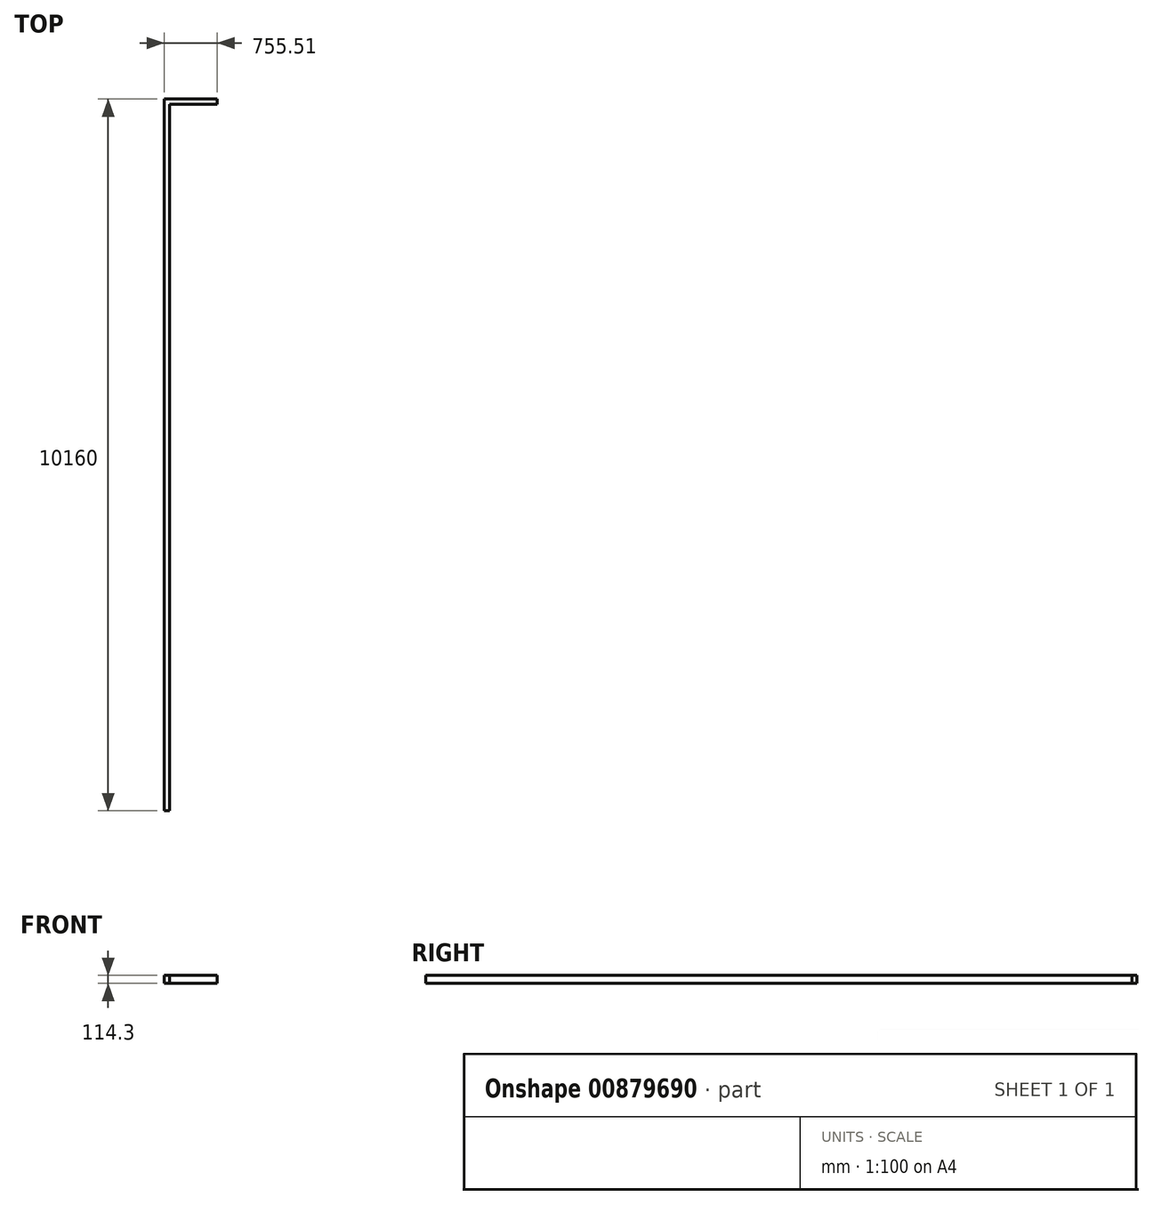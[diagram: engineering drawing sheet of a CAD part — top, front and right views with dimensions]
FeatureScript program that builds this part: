
annotation { "Feature Type Name" : "Feature", "Feature Type Description" : "" }
export const myFeature = defineFeature(function(context is Context, id is Id, definition is map)
    precondition{}
    {
        {
            var Q0;
            Q0=qCreatedBy(makeId("Top.planeOp"),FACE);
            var sketch = newSketch(context, id + "F0", { "sketchPlane" : qUnion([Q0])});
            skLineSegment(sketch, "E0", {"start": v(0, -963.04) * mm, "end": v(0, 9120.76) * mm});
            skLineSegment(sketch, "E1", {"start": v(0, 9120.76) * mm, "end": v(679.31, 9120.76) * mm});
            skLineSegment(sketch, "E2", {"start": v(679.31, 9120.76) * mm, "end": v(679.31, 9196.96) * mm});
            skLineSegment(sketch, "E3", {"start": v(679.31, 9196.96) * mm, "end": v(-76.2, 9196.96) * mm});
            skLineSegment(sketch, "E4", {"start": v(-76.2, 9196.96) * mm, "end": v(-76.2, -963.04) * mm});
            skLineSegment(sketch, "E5", {"start": v(-76.2, -963.04) * mm, "end": v(0, -963.04) * mm});
            skSolve(sketch);
        }
        {
            var Q0;
            Q0=makeQuery(id+"F0.imprint","IMPRINT",FACE,{"disambiguationData":[TD([[makeQuery(id+"F0.imprint","IMPRINT",EDGE,{"derivedFrom":sQuery(id+"F0.wireOp",EDGE,"E0")}),1.0]])]});
            extrude(context, id + "F1", {"entities" : qUnion([Q0]), "depth" : 114.3 * mm, "offsetDistance" : 25.4 * mm});
        }
    });
